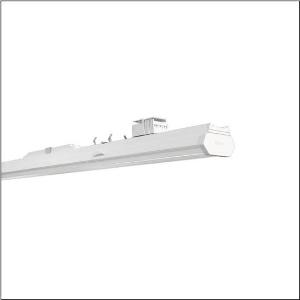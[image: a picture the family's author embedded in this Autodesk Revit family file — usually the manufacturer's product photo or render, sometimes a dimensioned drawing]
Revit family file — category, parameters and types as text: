
# Revit family: licross_r__11_protected_ho_51tp11dn4f5s_1ce9
name_source: partatom
category: Lighting Fixtures
units: mm (PartAtom-declared; Revit-internal decimal feet)

## family parameters
Cut with Voids When Loaded = No
Host = Face
Light Source = No
Part Type = Normal
Room Calculation Point = No
Round Connector Dimension = Use Diameter
Shared = No

## types (1)
- --- (1 x LED, 15510 lm, 87.3 W, 4000K)
    Apparent Load = 87 VA
    CIE Flux Codes = 84 94 98 99 100
    Color Rendering = 80
    Color Temperature = 4000K
    Default Elevation = 1800 mm
    Description = Licross® 11 Protected HO, luminaire insert, of sheet steel, galvanised, coil coated, white, length: 1.500mm, width: 90mm, height: 101mm, LED rated luminous flux: 15.510lm, light colour: 840, control gear: DALI 2, with plug, 5-pole, with phase selection, mains connection: 220..240V, AC, 50/60Hz, rated input power: 87W, halogen-free wiring, primary light control with lens, of plastic, primary optical cover: cover, of PMMA, light emission: direct distribution, primary light characteristic: symmetric, protection rating (complete): IP64, insulation class (complete): insulation class I (protective earthing), certification: CE, ENEC, VDE, UKCA, protection symbol: D if used in an environment with conductive dust loads with corresponding accessories, impact resistance: IK06, permissible ambient temperature for indoor applications: -25..+30°C, corresponds to IFS (International Featured Standards) requirements for safety and quality in the food industry, reducing of maximum allowable ambient temperature of 5°C with ceiling mounting, LABS conformity tested according to VDMA 24364:2018-05, packaging unit: 1 piece
    Height = 92 mm
    Lamp = 1 x LED
    Lamp Light Flux = 15510 lm
    Lamp Power = 87.3 W
    Lamp count = 1
    Length = 1500 mm
    Luminous efficacy = 178 lm/W
    Manufacturer = Siteco
    ModVariant = No
    Model = 51TP11DN4F5S
    Mounting Place = Ceiling
    Mounting Type = Pendant
    Number of Poles = 1
    OnlyDefault = Yes
    Power Factor = 1
    Product Name = Licross® 11 Protected HO
    Product group = luminaire insert
    ProductGroupID = 901
    Protection Class = Protection class I
    Protection Degree = IP 64
    RLX_Detail_Level = 1
    RLX_Emergency_Light_Flux = 0 lm
    RLX_Emergency_Type = 0
    RLX_Emergency_Type_DB = No
    RlxData = <blob elided: 24285 chars, md5=885767a0>
    Socket = socket
    Standby Power = 0 W
    System Light Flux = 15510 lm
    System Power = 87 W
    Type Comments = factory setting: luminous flux: 100 % | dim-lin: 254 | 589 mA
    Type Image = l_1256148.jpg
    URL = http://relux.com
    VarID = @adj_031141
    Voltage = 0 V
    Weight = 0.00 kg
    Width = 88 mm

## geometry (parser evidence)
native form markers: Blend x4, Sweep x11
no freeform markers — native parametric forms only
